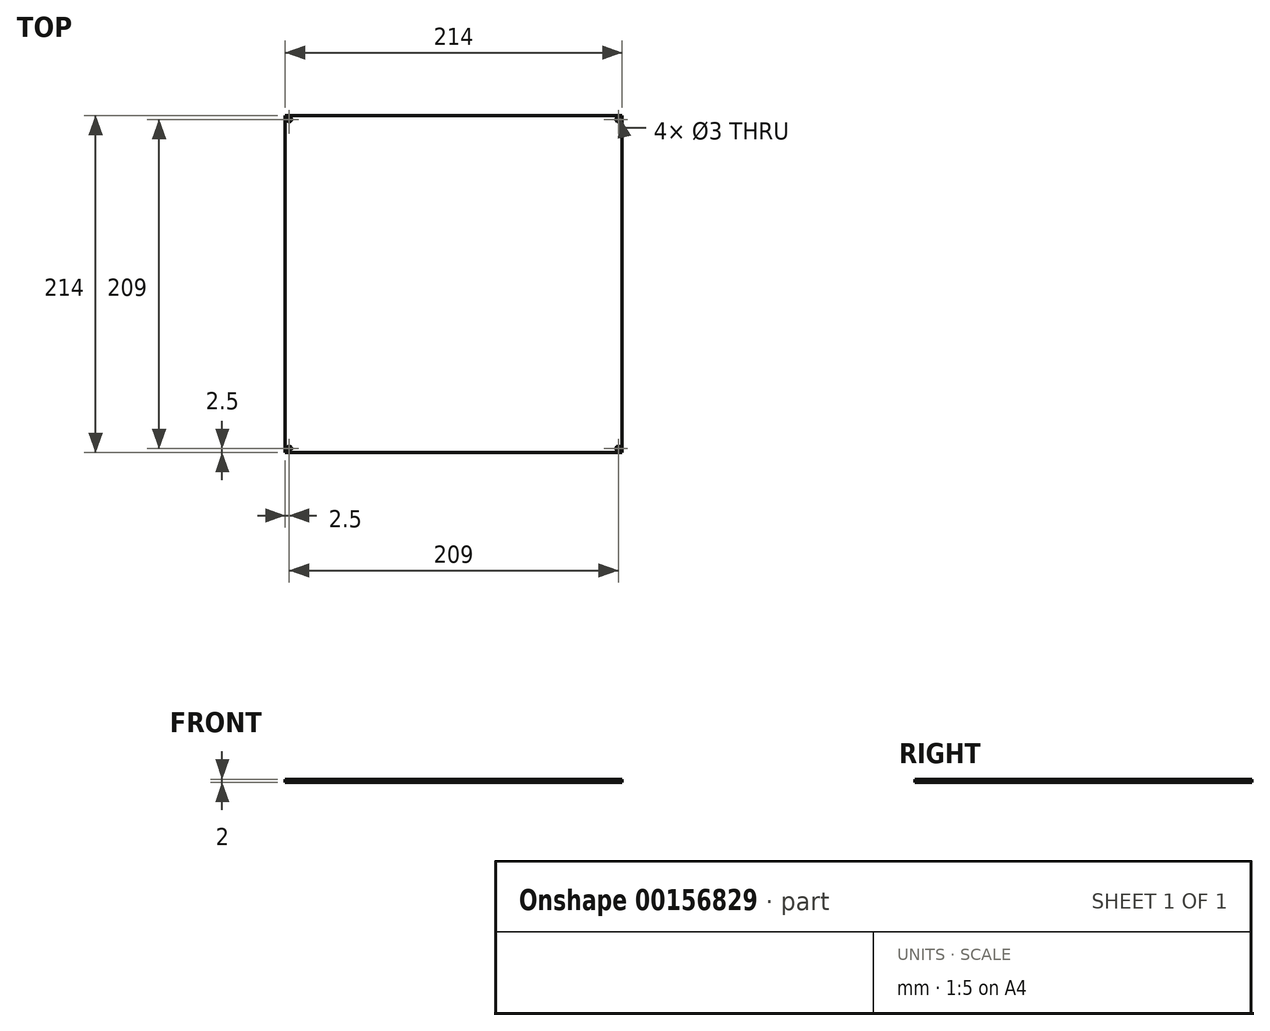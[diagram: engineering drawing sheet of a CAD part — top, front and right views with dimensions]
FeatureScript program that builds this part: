
annotation { "Feature Type Name" : "Feature", "Feature Type Description" : "" }
export const myFeature = defineFeature(function(context is Context, id is Id, definition is map)
    precondition{}
    {
        {
            var Q0;
            Q0=qCreatedBy(makeId("Top.planeOp"),FACE);
            var sketch = newSketch(context, id + "F0", { "sketchPlane" : qUnion([Q0])});
            skLineSegment(sketch, "E0.bottom", {"start": v(107, -107) * mm, "end": v(-107, -107) * mm});
            skLineSegment(sketch, "E0.top", {"start": v(107, 107) * mm, "end": v(-107, 107) * mm});
            skLineSegment(sketch, "E0.left", {"start": v(107, -107) * mm, "end": v(107, 107) * mm});
            skLineSegment(sketch, "E0.right", {"start": v(-107, -107) * mm, "end": v(-107, 107) * mm});
            skPoint(sketch, "E0.middle", {"position": v(0, 0) * mm});
            skCircle(sketch, "E1", {"center": v(-104.5, -104.5) * mm, "radius": 1.5 * mm});
            skCircle(sketch, "E2.0.1.0", {"center": v(-104.5, 104.5) * mm, "radius": 1.5 * mm});
            skCircle(sketch, "E2.1.0.0", {"center": v(104.5, -104.5) * mm, "radius": 1.5 * mm});
            skCircle(sketch, "E2.1.1.0", {"center": v(104.5, 104.5) * mm, "radius": 1.5 * mm});
            skLineSegment(sketch, "E2.direction1", {"start": v(-104.5, -104.5) * mm, "end": v(104.5, -104.5) * mm, "construction": true});
            skLineSegment(sketch, "E2.direction2", {"start": v(-104.5, -104.5) * mm, "end": v(-104.5, 104.5) * mm, "construction": true});
            skSolve(sketch);
        }
        {
            var Q0;
            Q0 = qSketchRegion(id + "F0", true);
            extrude(context, id + "F1", {"entities" : qUnion([Q0]), "depth" : 2 * mm});
        }
    });
